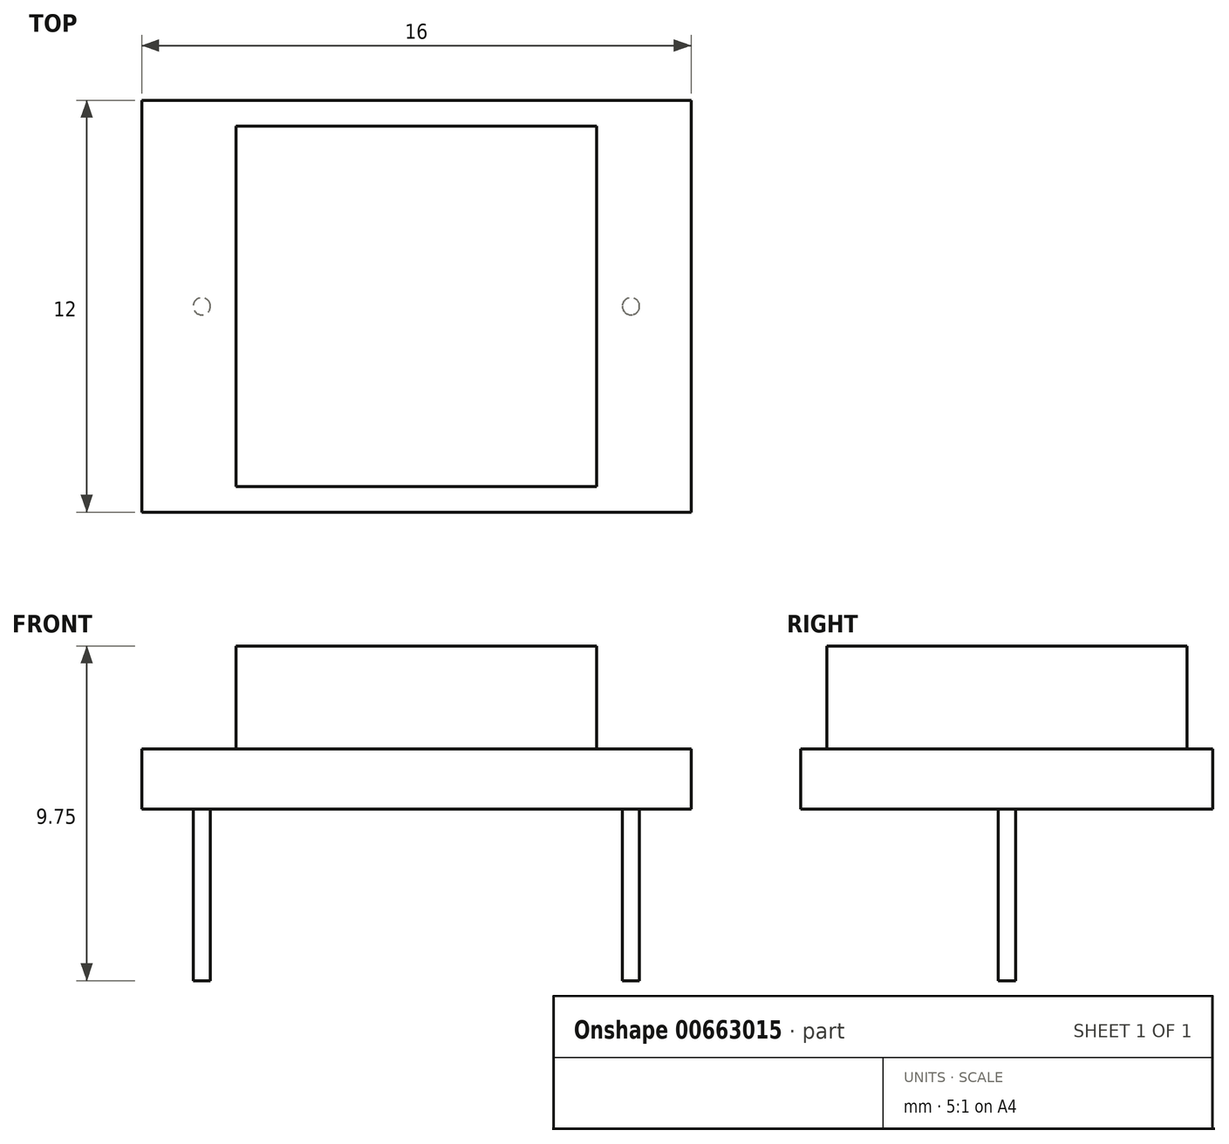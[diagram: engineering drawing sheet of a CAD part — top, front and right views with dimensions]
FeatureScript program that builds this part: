
annotation { "Feature Type Name" : "Feature", "Feature Type Description" : "" }
export const myFeature = defineFeature(function(context is Context, id is Id, definition is map)
    precondition{}
    {
        {
            var Q0;
            Q0=qCreatedBy(makeId("Top.planeOp"),FACE);
            var sketch = newSketch(context, id + "F0", { "sketchPlane" : qUnion([Q0])});
            skLineSegment(sketch, "E0.bottom", {"start": v(8, -6) * mm, "end": v(-8, -6) * mm});
            skLineSegment(sketch, "E0.top", {"start": v(8, 6) * mm, "end": v(-8, 6) * mm});
            skLineSegment(sketch, "E0.left", {"start": v(8, -6) * mm, "end": v(8, 6) * mm});
            skLineSegment(sketch, "E0.right", {"start": v(-8, -6) * mm, "end": v(-8, 6) * mm});
            skPoint(sketch, "E0.middle", {"position": v(0, 0) * mm});
            skSolve(sketch);
        }
        {
            var Q0;
            Q0=makeQuery(id+"F0.imprint","IMPRINT",FACE,{"disambiguationData":[TD([[makeQuery(id+"F0.imprint","IMPRINT",EDGE,{"derivedFrom":sQuery(id+"F0.wireOp",EDGE,"E0.bottom")}),-1.0]])]});
            extrude(context, id + "F1", {"entities" : qUnion([Q0]), "depth" : 1.75 * mm, "offsetDistance" : 25 * mm});
        }
        {
            var Q0;
            Q0=makeQuery(id+"F1.opExtrude","CAP_FACE",FACE,{"disambiguationData":[OSD([sQuery(id+"F0.wireOp",EDGE,"E0.bottom"),sQuery(id+"F0.wireOp",EDGE,"E0.top"),sQuery(id+"F0.wireOp",EDGE,"E0.left"),sQuery(id+"F0.wireOp",EDGE,"E0.right")])],"isStart":false});
            var sketch = newSketch(context, id + "F2", { "sketchPlane" : qUnion([Q0])});
            skLineSegment(sketch, "E1.bottom", {"start": v(5.25, -5.25) * mm, "end": v(-5.25, -5.25) * mm});
            skLineSegment(sketch, "E1.top", {"start": v(5.25, 5.25) * mm, "end": v(-5.25, 5.25) * mm});
            skLineSegment(sketch, "E1.left", {"start": v(5.25, -5.25) * mm, "end": v(5.25, 5.25) * mm});
            skLineSegment(sketch, "E1.right", {"start": v(-5.25, -5.25) * mm, "end": v(-5.25, 5.25) * mm});
            skPoint(sketch, "E1.middle", {"position": v(0, 0) * mm});
            skSolve(sketch);
        }
        {
            var Q0;
            Q0=makeQuery(id+"F2.imprint","IMPRINT",FACE,{"disambiguationData":[TD([[makeQuery(id+"F2.imprint","IMPRINT",EDGE,{"derivedFrom":sQuery(id+"F2.wireOp",EDGE,"E1.bottom")}),-1.0]])]});
            extrude(context, id + "F3", {"entities" : qUnion([Q0]), "operationType" : NewBodyOperationType.ADD, "depth" : 3 * mm, "offsetDistance" : 25 * mm});
        }
        {
            var Q0;
            Q0=makeQuery(id+"F1.opExtrude","CAP_FACE",FACE,{"disambiguationData":[OSD([sQuery(id+"F0.wireOp",EDGE,"E0.bottom"),sQuery(id+"F0.wireOp",EDGE,"E0.top"),sQuery(id+"F0.wireOp",EDGE,"E0.left"),sQuery(id+"F0.wireOp",EDGE,"E0.right")])],"isStart":true});
            var sketch = newSketch(context, id + "F4", { "sketchPlane" : qUnion([Q0])});
            skCircle(sketch, "E2", {"center": v(-6.25, 0) * mm, "radius": 0.25 * mm});
            skCircle(sketch, "E3", {"center": v(6.25, 0) * mm, "radius": 0.25 * mm});
            skLineSegment(sketch, "E4", {"start": v(-8, 0) * mm, "end": v(-6.25, 0) * mm, "construction": true});
            skLineSegment(sketch, "E5", {"start": v(6.25, 0) * mm, "end": v(8, 0) * mm, "construction": true});
            skSolve(sketch);
        }
        {
            var Q0;
            Q0=makeQuery(id+"F4.imprint","IMPRINT",FACE,{"disambiguationData":[TD([[makeQuery(id+"F4.imprint","IMPRINT",EDGE,{"derivedFrom":sQuery(id+"F4.wireOp",EDGE,"E2")}),1.0]])]});
            var Q1;
            Q1=makeQuery(id+"F4.imprint","IMPRINT",FACE,{"disambiguationData":[TD([[makeQuery(id+"F4.imprint","IMPRINT",EDGE,{"derivedFrom":sQuery(id+"F4.wireOp",EDGE,"E3")}),1.0]])]});
            extrude(context, id + "F5", {"entities" : qUnion([Q0, Q1]), "operationType" : NewBodyOperationType.ADD, "depth" : 5 * mm, "offsetDistance" : 25 * mm});
        }
    });
